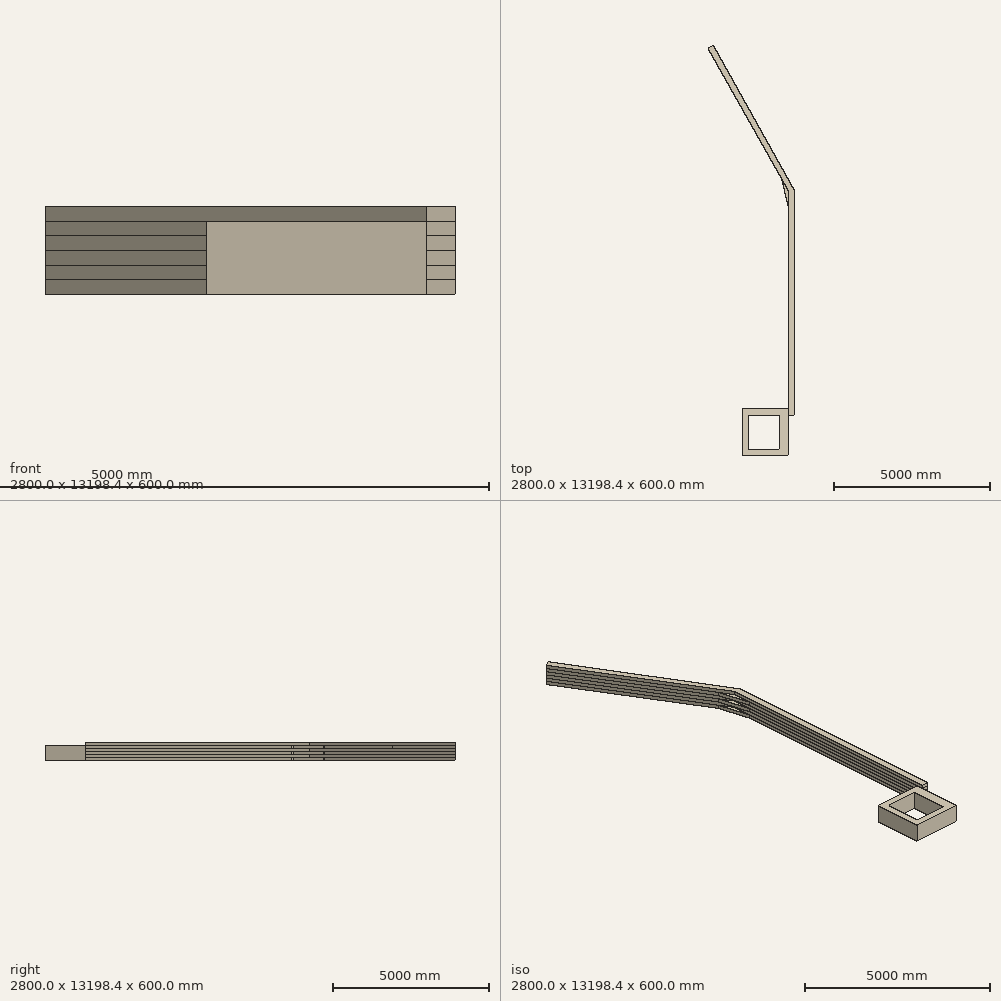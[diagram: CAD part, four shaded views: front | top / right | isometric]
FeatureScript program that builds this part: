
annotation { "Feature Type Name" : "Feature", "Feature Type Description" : "" }
export const myFeature = defineFeature(function(context is Context, id is Id, definition is map)
    precondition{}
    {
        {
            var Q0;
            Q0=qCreatedBy(makeId("Top.planeOp"),FACE);
            var sketch = newSketch(context, id + "F0", { "sketchPlane" : qUnion([Q0])});
            skLineSegment(sketch, "E0.bottom", {"start": v(0, 0) * mm, "end": v(-1500, 0) * mm});
            skLineSegment(sketch, "E0.top", {"start": v(0, -1500) * mm, "end": v(-1500, -1500) * mm});
            skLineSegment(sketch, "E0.left", {"start": v(0, 0) * mm, "end": v(0, -1500) * mm});
            skLineSegment(sketch, "E0.right", {"start": v(-1500, 0) * mm, "end": v(-1500, -1500) * mm});
            skLineSegment(sketch, "E1.bottom", {"start": v(-300, -200) * mm, "end": v(-1300, -200) * mm});
            skLineSegment(sketch, "E1.top", {"start": v(-300, -1300) * mm, "end": v(-1300, -1300) * mm});
            skLineSegment(sketch, "E1.left", {"start": v(-300, -200) * mm, "end": v(-300, -1300) * mm});
            skLineSegment(sketch, "E1.right", {"start": v(-1300, -200) * mm, "end": v(-1300, -1300) * mm});
            skSolve(sketch);
        }
        {
            var Q0;
            Q0=makeQuery(id+"F0.imprint","IMPRINT",FACE,{"disambiguationData":[TD([[makeQuery(id+"F0.imprint","IMPRINT",EDGE,{"derivedFrom":sQuery(id+"F0.wireOp",EDGE,"E0.bottom")}),1.0]])]});
            extrude(context, id + "F1", {"entities" : qUnion([Q0]), "oppositeDirection" : true, "depth" : 500 * mm, "offsetDistance" : 25.4 * mm});
        }
        {
            var Q0;
            Q0=qCreatedBy(makeId("Top.planeOp"),FACE);
            var sketch = newSketch(context, id + "F2", { "sketchPlane" : qUnion([Q0])});
            skLineSegment(sketch, "E2.bottom", {"start": v(0, -200) * mm, "end": v(200, -200) * mm});
            skLineSegment(sketch, "E2.top", {"start": v(0, 7000) * mm, "end": v(200, 7000) * mm});
            skLineSegment(sketch, "E2.left", {"start": v(0, -200) * mm, "end": v(0, 7000) * mm});
            skLineSegment(sketch, "E2.right", {"start": v(200, -200) * mm, "end": v(200, 7000) * mm});
            skLineSegment(sketch, "E3", {"start": v(0, 7000) * mm, "end": v(-2600, 11600) * mm});
            skLineSegment(sketch, "E4", {"start": v(-2600, 11600) * mm, "end": v(-2425.89, 11698.41) * mm});
            skLineSegment(sketch, "E5", {"start": v(-2425.89, 11698.41) * mm, "end": v(200, 7000) * mm});
            skSolve(sketch);
        }
        {
            var Q0;
            Q0=makeQuery(id+"F2.imprint","IMPRINT",FACE,{"disambiguationData":[TD([[makeQuery(id+"F2.imprint","IMPRINT",EDGE,{"derivedFrom":sQuery(id+"F2.wireOp",EDGE,"E2.bottom")}),1.0]])]});
            var Q1;
            Q1=makeQuery(id+"F2.imprint","IMPRINT",FACE,{"disambiguationData":[TD([[makeQuery(id+"F2.imprint","IMPRINT",EDGE,{"derivedFrom":sQuery(id+"F2.wireOp",EDGE,"E2.top")}),1.0]])]});
            extrude(context, id + "F3", {"entities" : qUnion([Q0, Q1]), "depth" : 100 * mm, "offsetDistance" : 25 * mm});
        }
        {
            var Q0;
            Q0=makeQuery(id+"F3.opExtrude","CAP_FACE",FACE,{"disambiguationData":[OSD([sQuery(id+"F2.wireOp",EDGE,"E2.bottom"),sQuery(id+"F2.wireOp",EDGE,"E2.left"),sQuery(id+"F2.wireOp",EDGE,"E2.right"),sQuery(id+"F2.wireOp",EDGE,"E3"),sQuery(id+"F2.wireOp",EDGE,"E4"),sQuery(id+"F2.wireOp",EDGE,"E5")])],"isStart":true});
            var sketch = newSketch(context, id + "F4", { "sketchPlane" : qUnion([Q0])});
            skLineSegment(sketch, "E6", {"start": v(0, -6430.56) * mm, "end": v(-228.42, -7404.13) * mm});
            skLineSegment(sketch, "E7", {"start": v(-228.42, -7404.13) * mm, "end": v(-33.7, -7449.81) * mm});
            skLineSegment(sketch, "E8", {"start": v(-33.7, -7449.81) * mm, "end": v(194.71, -6476.25) * mm});
            skLineSegment(sketch, "E9", {"start": v(194.71, -6476.25) * mm, "end": v(0, -6430.56) * mm});
            skLineSegment(sketch, "E10", {"start": v(-617.12, -6785.05) * mm, "end": v(200, -7000) * mm, "construction": true});
            skPoint(sketch, "E11", {"position": v(-114.2, -6917.35) * mm});
            skSolve(sketch);
        }
        {
            var Q0;
            Q0 = qSketchRegion(id + "F4", true);
            extrude(context, id + "F5", {"entities" : qUnion([Q0]), "operationType" : NewBodyOperationType.ADD, "depth" : 100 * mm, "offsetDistance" : 25 * mm});
        }
        {
            var Q0;
            {var subQ2=sQuery(id+"F4.wireOp",EDGE,"E9");Q0=makeQuery(id+"F4.imprint","IMPRINT",FACE,{"disambiguationData":[TD([[makeQuery(id+"F4.imprint","IMPRINT",EDGE,{"derivedFrom":subQ2}),-1.0]])]});}
            var sketch = newSketch(context, id + "F6", { "sketchPlane" : qUnion([Q0])});
            skLineSegment(sketch, "E12.bottom", {"start": v(0, -6430.56) * mm, "end": v(200, -6430.56) * mm});
            skLineSegment(sketch, "E12.top", {"start": v(0, -3930.56) * mm, "end": v(200, -3930.56) * mm});
            skLineSegment(sketch, "E12.left", {"start": v(0, -6430.56) * mm, "end": v(0, -3930.56) * mm});
            skLineSegment(sketch, "E12.right", {"start": v(200, -6430.56) * mm, "end": v(200, -3930.56) * mm});
            skLineSegment(sketch, "E13.top", {"start": v(0, -1430.56) * mm, "end": v(200, -1430.56) * mm});
            skLineSegment(sketch, "E13.left", {"start": v(0, -3930.56) * mm, "end": v(0, -1430.56) * mm});
            skLineSegment(sketch, "E13.right", {"start": v(200, -3930.56) * mm, "end": v(200, -1430.56) * mm});
            skLineSegment(sketch, "E14.bottom", {"start": v(200, -1430.56) * mm, "end": v(0, -1430.56) * mm});
            skLineSegment(sketch, "E14.top", {"start": v(200, 200) * mm, "end": v(0, 200) * mm});
            skLineSegment(sketch, "E14.left", {"start": v(200, -1430.56) * mm, "end": v(200, 200) * mm});
            skLineSegment(sketch, "E14.right", {"start": v(0, -1430.56) * mm, "end": v(0, 200) * mm});
            skLineSegment(sketch, "E15", {"start": v(-228.42, -7404.13) * mm, "end": v(-1458.56, -9580.53) * mm});
            skLineSegment(sketch, "E16", {"start": v(-1458.56, -9580.53) * mm, "end": v(-1304.63, -9667.54) * mm});
            skLineSegment(sketch, "E17", {"start": v(-1304.63, -9667.54) * mm, "end": v(-74.49, -7491.13) * mm});
            skLineSegment(sketch, "E18", {"start": v(-74.49, -7491.13) * mm, "end": v(-228.42, -7404.13) * mm});
            skLineSegment(sketch, "E19", {"start": v(-1458.56, -9580.53) * mm, "end": v(-2600, -11600) * mm});
            skLineSegment(sketch, "E20", {"start": v(-2600, -11600) * mm, "end": v(-2425.89, -11698.41) * mm});
            skLineSegment(sketch, "E21", {"start": v(-2425.89, -11698.41) * mm, "end": v(-1304.63, -9667.54) * mm});
            skSolve(sketch);
        }
        {
            var Q0;
            Q0 = qSketchRegion(id + "F6", true);
            extrude(context, id + "F7", {"entities" : qUnion([Q0]), "depth" : 100 * mm, "offsetDistance" : 25 * mm});
        }
        {
            var Q0;
            Q0=makeQuery(id+"F5.opExtrude","CAP_FACE",FACE,{"disambiguationData":[OSD([sQuery(id+"F4.wireOp",EDGE,"E6"),sQuery(id+"F4.wireOp",EDGE,"E7"),sQuery(id+"F4.wireOp",EDGE,"E8"),sQuery(id+"F4.wireOp",EDGE,"E9")])],"isStart":false});
            var sketch = newSketch(context, id + "F8", { "sketchPlane" : qUnion([Q0])});
            skLineSegment(sketch, "E22.0", {"start": v(200, 200) * mm, "end": v(200, -7000) * mm});
            skLineSegment(sketch, "E23.0", {"start": v(0, 200) * mm, "end": v(0, -7000) * mm});
            skLineSegment(sketch, "E24.0", {"start": v(0, 200) * mm, "end": v(200, 200) * mm});
            skLineSegment(sketch, "E25.0", {"start": v(-2425.89, -11698.41) * mm, "end": v(200, -7000) * mm});
            skLineSegment(sketch, "E26.0", {"start": v(-2600, -11600) * mm, "end": v(-2425.89, -11698.41) * mm});
            skLineSegment(sketch, "E27.0", {"start": v(0, -7000) * mm, "end": v(-2600, -11600) * mm});
            skSolve(sketch);
        }
        {
            var Q0;
            Q0 = qSketchRegion(id + "F8", true);
            extrude(context, id + "F9", {"entities" : qUnion([Q0]), "depth" : 100 * mm, "offsetDistance" : 25 * mm});
        }
        {
            var Q0;
            Q0=makeQuery(id+"F9.opExtrude","CAP_FACE",FACE,{"disambiguationData":[OSD([sQuery(id+"F8.wireOp",EDGE,"E22.0"),sQuery(id+"F8.wireOp",EDGE,"E23.0"),sQuery(id+"F8.wireOp",EDGE,"E24.0"),sQuery(id+"F8.wireOp",EDGE,"E25.0"),sQuery(id+"F8.wireOp",EDGE,"E26.0"),sQuery(id+"F8.wireOp",EDGE,"E27.0")])],"isStart":false});
            var sketch = newSketch(context, id + "F10", { "sketchPlane" : qUnion([Q0])});
            skLineSegment(sketch, "E28.0", {"start": v(0, 200) * mm, "end": v(0, -6430.56) * mm});
            skLineSegment(sketch, "E29.0", {"start": v(0, -6430.56) * mm, "end": v(-228.42, -7404.13) * mm});
            skLineSegment(sketch, "E30.0", {"start": v(-228.42, -7404.13) * mm, "end": v(-2600, -11600) * mm});
            skLineSegment(sketch, "E31.0", {"start": v(-2600, -11600) * mm, "end": v(-2425.89, -11698.41) * mm});
            skLineSegment(sketch, "E32.0", {"start": v(-2425.89, -11698.41) * mm, "end": v(-74.49, -7491.13) * mm});
            skLineSegment(sketch, "E33.0", {"start": v(-33.7, -7449.81) * mm, "end": v(194.71, -6476.25) * mm});
            skLineSegment(sketch, "E34.0", {"start": v(-228.42, -7404.13) * mm, "end": v(-33.7, -7449.81) * mm});
            skLineSegment(sketch, "E35.4", {"start": v(200, 200) * mm, "end": v(200, -6430.56) * mm});
            skLineSegment(sketch, "E35.8", {"start": v(200, 200) * mm, "end": v(200, -6430.56) * mm});
            skLineSegment(sketch, "E35.9", {"start": v(200, 200) * mm, "end": v(200, -6430.56) * mm});
            skLineSegment(sketch, "E36.0", {"start": v(-74.49, -7491.13) * mm, "end": v(-228.42, -7404.13) * mm});
            skLineSegment(sketch, "E37.0", {"start": v(194.71, -6476.25) * mm, "end": v(0, -6430.56) * mm});
            skLineSegment(sketch, "E38.0", {"start": v(0, -6430.56) * mm, "end": v(200, -6430.56) * mm});
            skLineSegment(sketch, "E39.0", {"start": v(0, 200) * mm, "end": v(200, 200) * mm});
            skPoint(sketch, "E40.orphan", {"position": v(200, -7000) * mm});
            skSolve(sketch);
        }
        {
            var Q0;
            Q0 = qSketchRegion(id + "F10", true);
            extrude(context, id + "F11", {"entities" : qUnion([Q0]), "depth" : 100 * mm, "offsetDistance" : 25 * mm});
        }
        {
            var Q0;
            Q0=makeQuery(id+"F11.opExtrude","CAP_FACE",FACE,{"disambiguationData":[OSD([sQuery(id+"F10.wireOp",EDGE,"E29.0"),sQuery(id+"F10.wireOp",EDGE,"E33.0"),sQuery(id+"F10.wireOp",EDGE,"E34.0"),sQuery(id+"F10.wireOp",EDGE,"E37.0")])],"isStart":false});
            var sketch = newSketch(context, id + "F12", { "sketchPlane" : qUnion([Q0])});
            skLineSegment(sketch, "E41.0", {"start": v(0, -7000) * mm, "end": v(-2600, -11600) * mm});
            skLineSegment(sketch, "E42.0", {"start": v(0, 200) * mm, "end": v(0, -7000) * mm});
            skLineSegment(sketch, "E43.0", {"start": v(0, 200) * mm, "end": v(200, 200) * mm});
            skLineSegment(sketch, "E44.0", {"start": v(200, 200) * mm, "end": v(200, -7000) * mm});
            skLineSegment(sketch, "E45.0", {"start": v(-2425.89, -11698.41) * mm, "end": v(200, -7000) * mm});
            skLineSegment(sketch, "E46.0", {"start": v(-2600, -11600) * mm, "end": v(-2425.89, -11698.41) * mm});
            skSolve(sketch);
        }
        {
            var Q0;
            Q0 = qSketchRegion(id + "F12", true);
            extrude(context, id + "F13", {"entities" : qUnion([Q0]), "depth" : 100 * mm, "offsetDistance" : 25 * mm});
        }
        {
            var Q0;
            Q0=makeQuery(id+"F13.opExtrude","CAP_FACE",FACE,{"disambiguationData":[OSD([sQuery(id+"F12.wireOp",EDGE,"E41.0"),sQuery(id+"F12.wireOp",EDGE,"E42.0"),sQuery(id+"F12.wireOp",EDGE,"E43.0"),sQuery(id+"F12.wireOp",EDGE,"E44.0"),sQuery(id+"F12.wireOp",EDGE,"E45.0"),sQuery(id+"F12.wireOp",EDGE,"E46.0")])],"isStart":false});
            var sketch = newSketch(context, id + "F14", { "sketchPlane" : qUnion([Q0])});
            skLineSegment(sketch, "E47.0", {"start": v(0, -6430.56) * mm, "end": v(-228.42, -7404.13) * mm});
            skLineSegment(sketch, "E48.0", {"start": v(-33.7, -7449.81) * mm, "end": v(194.71, -6476.25) * mm});
            skLineSegment(sketch, "E49.0", {"start": v(-2425.89, -11698.41) * mm, "end": v(-74.49, -7491.13) * mm});
            skLineSegment(sketch, "E50.0", {"start": v(200, 200) * mm, "end": v(200, -6430.56) * mm});
            skLineSegment(sketch, "E51", {"start": v(-228.42, -7404.13) * mm, "end": v(-33.7, -7449.81) * mm});
            skLineSegment(sketch, "E52", {"start": v(194.71, -6476.25) * mm, "end": v(0, -6430.56) * mm});
            skLineSegment(sketch, "E53.0", {"start": v(-2600, -11600) * mm, "end": v(-2425.89, -11698.41) * mm});
            skLineSegment(sketch, "E54.0", {"start": v(-228.42, -7404.13) * mm, "end": v(-2600, -11600) * mm});
            skPoint(sketch, "E55.orphan", {"position": v(0, -7000) * mm});
            skLineSegment(sketch, "E56", {"start": v(-74.49, -7491.13) * mm, "end": v(-228.42, -7404.13) * mm});
            skLineSegment(sketch, "E57", {"start": v(200, -6430.56) * mm, "end": v(0, -6430.56) * mm});
            skLineSegment(sketch, "E58.0", {"start": v(0, 200) * mm, "end": v(0, -6430.56) * mm});
            skLineSegment(sketch, "E59.0", {"start": v(0, 200) * mm, "end": v(200, 200) * mm});
            skSolve(sketch);
        }
        {
            var Q0;
            Q0 = qSketchRegion(id + "F14", true);
            extrude(context, id + "F15", {"entities" : qUnion([Q0]), "depth" : 100 * mm, "offsetDistance" : 25 * mm});
        }
    });
